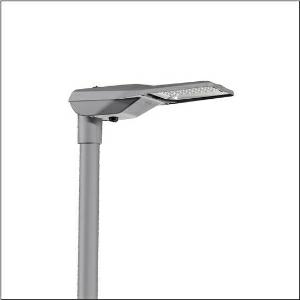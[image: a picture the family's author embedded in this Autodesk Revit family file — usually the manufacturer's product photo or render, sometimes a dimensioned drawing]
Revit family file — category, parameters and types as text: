
# Revit family: streetlight_sl_21_iq_mini___st1_0a_5xe2d41y08gb_5b29
name_source: partatom
category: Lighting Fixtures
units: mm (PartAtom-declared; Revit-internal decimal feet)

## family parameters
Cut with Voids When Loaded = No
Host = Face
Light Source = No
Part Type = Normal
Room Calculation Point = No
Round Connector Dimension = Use Diameter
Shared = No

## types (1)
- --- (1 x LED, 6190 lm, 39.8 W, 4000K)
    Apparent Load = 40 VA
    CIE Flux Codes = 37 72 97 100 100
    Color Rendering = 70
    Color Temperature = 4000K
    Default Elevation = 1800 mm
    Description = Streetlight SL 21 iQ mini, mast luminaire, primary light control with lens, of PMMA, primary optical cover: cover, of toughened safety glass, transparent, light distribution: ST1.0a, light emission: direct distribution, primary light characteristic: asymmetric, installation type: post-top, side-entry, LED, High Power LED, rated luminous flux: 6.190lm, luminous efficacy: 156lm/W, light colour: 740, colour temperature: 4000K, control gear: iQ-Street Remote, D4i with power reduction, control: pre-setting: logarithmic dimming characteristic, Street-Remote, Auto-Match, Temp-Guard, Lumen-Switch, Night-Set, Smart-Wire, Light-Fading, Desk-Remote (wireless, voltage-free reading and setting of iQ features in the workshop via application-optimized NFC function/RFID function), optimised constant luminous flux control (CLO 2.0), mains connection: 220..240V, AC, 50/60Hz, start of lifetime: 40W, end of service life: 41W, reduction: 18W, luminaire housing, of diecast aluminium, powder-coated, SITECO metallic grey (DB 702S), corrosivity category C5 high according to DIN EN ISO 12944, please order mast flange separately, inclination adjustable: 0°, 5°, 10°, 15°, sealing non-destructively replaceable, multi-level sealing system, length: 628mm, width: 235mm, height: 110mm, mast flange for spigot size: 42mm (side-entry): 5XC10008XM4, 60/48mm (side-entry/post-top): 5XC10108XM2, 76/60mm (side-entry/post-top): 5XC10108XM1, mounting height: 4..8m, Smart Interface below and above, protection rating (complete): IP66, insulation class (complete): insulation class II (safety insulation), certification: CE, ENEC, ENEC+, VDE, impact resistance: IK10, permissible operating ambient temperature for outdoor applications: -40..+50°C, standard-compliant lighting for roads and squares, packaging unit: 1 piece

Light Distribution: ST1.0a
    Height = 110 mm
    Lamp = 1 x LED
    Lamp Light Flux = 6190 lm
    Lamp Power = 39.8 W
    Lamp count = 1
    Length = 625 mm
    Luminous efficacy = 156 lm/W
    Manufacturer = Siteco
    ModVariant = No
    Model = 5XE2D41Y08GB
    Number of Poles = 1
    OnlyDefault = Yes
    Power Factor = 1
    Product Name = Streetlight SL 21 iQ mini | ST1.0a
    Product group = mast luminaire | pylon top
    ProductGroupID = 6100
    Protection Class = Protection class II
    Protection Degree = IP 66
    RLX_Detail_Level = 1
    RLX_Emergency_Light_Flux = 0 lm
    RLX_Emergency_Type = 0
    RLX_Emergency_Type_DB = No
    RlxData = <blob elided: 94025 chars, md5=3e17a285>
    Socket = socket
    Standby Power = 0 W
    System Light Flux = 6190 lm
    System Power = 40 W
    Type Comments = factory setting: luminous flux: 100 % | dim-lin: 254 | 800 mA
    Type Image = l_1003514.jpg
    URL = http://relux.com
    VarID = @adj_114881
    Voltage = 0 V
    Weight = 0.00 kg
    Width = 234 mm

## geometry (parser evidence)
native form markers: Blend x4, Sweep x12
no freeform markers — native parametric forms only
